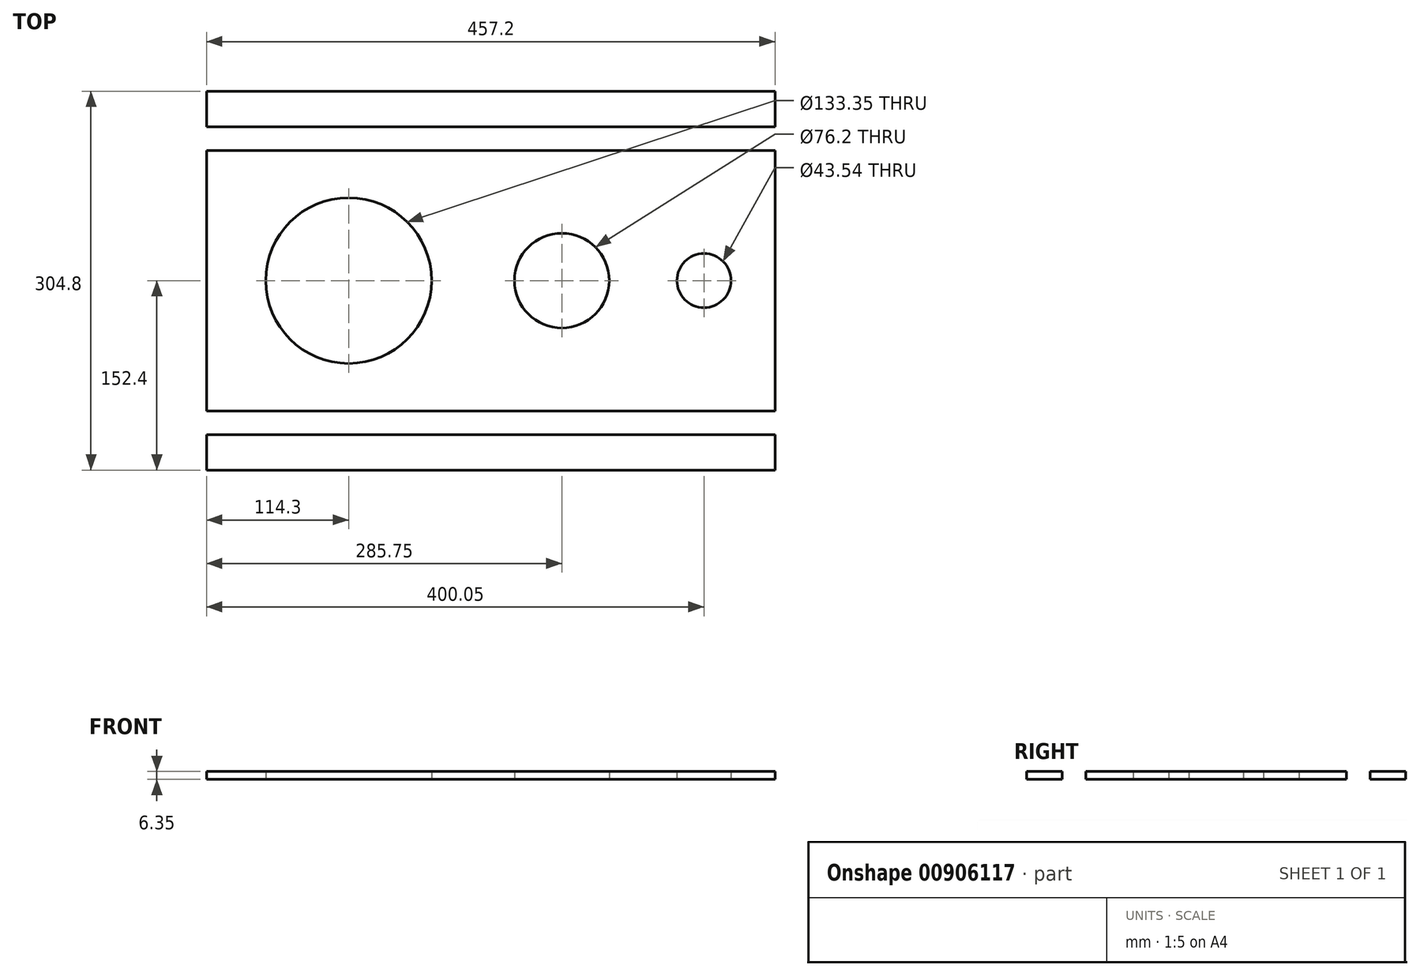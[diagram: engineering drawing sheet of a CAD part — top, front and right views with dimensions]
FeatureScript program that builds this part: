
annotation { "Feature Type Name" : "Feature", "Feature Type Description" : "" }
export const myFeature = defineFeature(function(context is Context, id is Id, definition is map)
    precondition{}
    {
        {
            var Q0;
            Q0=qCreatedBy(makeId("Top.planeOp"),FACE);
            var sketch = newSketch(context, id + "F0", { "sketchPlane" : qUnion([Q0])});
            skCircle(sketch, "E0", {"center": v(0, 0) * mm, "radius": 25.4 * mm, "construction": true});
            skCircle(sketch, "E1.cCircle", {"center": v(0, 0) * mm, "radius": 42.94 * mm, "construction": true});
            skLineSegment(sketch, "E1.0", {"start": v(0, 44.45) * mm, "end": v(22.22, 38.5) * mm, "construction": true});
            skLineSegment(sketch, "E1.1", {"start": v(22.22, 38.5) * mm, "end": v(38.5, 22.23) * mm, "construction": true});
            skLineSegment(sketch, "E1.2", {"start": v(38.5, 22.22) * mm, "end": v(44.45, 0) * mm, "construction": true});
            skLineSegment(sketch, "E1.3", {"start": v(44.45, 0) * mm, "end": v(38.5, -22.22) * mm, "construction": true});
            skLineSegment(sketch, "E1.4", {"start": v(38.5, -22.22) * mm, "end": v(22.23, -38.5) * mm, "construction": true});
            skLineSegment(sketch, "E1.5", {"start": v(22.23, -38.5) * mm, "end": v(0, -44.45) * mm, "construction": true});
            skLineSegment(sketch, "E1.6", {"start": v(0, -44.45) * mm, "end": v(-22.22, -38.5) * mm, "construction": true});
            skLineSegment(sketch, "E1.7", {"start": v(-22.22, -38.5) * mm, "end": v(-38.5, -22.23) * mm, "construction": true});
            skLineSegment(sketch, "E1.8", {"start": v(-38.5, -22.23) * mm, "end": v(-44.45, 0) * mm, "construction": true});
            skLineSegment(sketch, "E1.9", {"start": v(-44.45, 0) * mm, "end": v(-38.5, 22.22) * mm, "construction": true});
            skLineSegment(sketch, "E1.10", {"start": v(-38.5, 22.22) * mm, "end": v(-22.22, 38.5) * mm, "construction": true});
            skLineSegment(sketch, "E1.11", {"start": v(-22.22, 38.5) * mm, "end": v(0, 44.45) * mm, "construction": true});
            skPoint(sketch, "E1.0.midPoint", {"position": v(11.11, 41.47) * mm});
            skCircle(sketch, "E2", {"center": v(22.22, 38.5) * mm, "radius": 9.53 * mm, "construction": true});
            skCircle(sketch, "E3", {"center": v(38.5, 22.23) * mm, "radius": 9.53 * mm, "construction": true});
            skCircle(sketch, "E4", {"center": v(44.45, 0) * mm, "radius": 9.53 * mm, "construction": true});
            skCircle(sketch, "E5", {"center": v(38.5, -22.22) * mm, "radius": 9.53 * mm, "construction": true});
            skCircle(sketch, "E6", {"center": v(22.23, -38.5) * mm, "radius": 9.53 * mm, "construction": true});
            skPoint(sketch, "E7.startSnap0", {"position": v(-41.47, 11.11) * mm});
            skArc(sketch, "E8", {"start": v(0, 45.72) * mm, "mid": v(-45.72, 0) * mm, "end": v(0, -45.72) * mm, "construction": true});
            skArc(sketch, "E9.0.startCap", {"start": v(0, 55.25) * mm, "mid": v(9.53, 45.72) * mm, "end": v(0, 36.2) * mm, "construction": true});
            skArc(sketch, "E9.0.endCap", {"start": v(0, -36.2) * mm, "mid": v(9.53, -45.72) * mm, "end": v(0, -55.25) * mm, "construction": true});
            skArc(sketch, "E9.0.left", {"start": v(0, 36.2) * mm, "mid": v(-36.2, 0) * mm, "end": v(0, -36.2) * mm, "construction": true});
            skArc(sketch, "E9.0.right", {"start": v(0, 55.25) * mm, "mid": v(-55.25, 0) * mm, "end": v(0, -55.25) * mm, "construction": true});
            skCircle(sketch, "E10", {"center": v(0, 0) * mm, "radius": 66.68 * mm});
            skCircle(sketch, "E11.0", {"center": v(0, 0) * mm, "radius": 73.03 * mm});
            skLineSegment(sketch, "E12.bottom", {"start": v(-114.3, 152.4) * mm, "end": v(107.95, 152.4) * mm});
            skLineSegment(sketch, "E12.top", {"start": v(-114.3, -152.4) * mm, "end": v(104.92, -152.4) * mm});
            skLineSegment(sketch, "E12.left", {"start": v(-114.3, 152.4) * mm, "end": v(-114.3, -152.4) * mm});
            skLineSegment(sketch, "E13", {"start": v(-114.3, 0) * mm, "end": v(114.3, 0) * mm, "construction": true});
            skLineSegment(sketch, "E14.bottom", {"start": v(107.95, 152.4) * mm, "end": v(342.9, 152.4) * mm});
            skLineSegment(sketch, "E14.top", {"start": v(104.92, -152.4) * mm, "end": v(342.9, -152.4) * mm});
            skLineSegment(sketch, "E14.right", {"start": v(342.9, 152.4) * mm, "end": v(342.9, -152.4) * mm});
            skLineSegment(sketch, "E15", {"start": v(342.9, 152.4) * mm, "end": v(495.3, 0) * mm});
            skLineSegment(sketch, "E16", {"start": v(495.3, 0) * mm, "end": v(342.9, -152.4) * mm});
            skLineSegment(sketch, "E17", {"start": v(-114.3, 123.83) * mm, "end": v(371.48, 123.83) * mm});
            skLineSegment(sketch, "E18", {"start": v(390.53, 104.78) * mm, "end": v(-114.3, 104.78) * mm});
            skLineSegment(sketch, "E19", {"start": v(-114.3, -104.77) * mm, "end": v(390.53, -104.77) * mm});
            skLineSegment(sketch, "E20", {"start": v(-114.3, -123.82) * mm, "end": v(371.48, -123.82) * mm});
            skLineSegment(sketch, "E21", {"start": v(114.3, 0) * mm, "end": v(495.3, 0) * mm, "construction": true});
            skCircle(sketch, "E22", {"center": v(171.45, 0) * mm, "radius": 38.1 * mm});
            skCircle(sketch, "E23", {"center": v(285.75, 0) * mm, "radius": 21.77 * mm});
            skCircle(sketch, "E24", {"center": v(387.35, 0) * mm, "radius": 12.7 * mm, "construction": true});
            skPoint(sketch, "E25", {"position": v(25.4, 0) * mm});
            skPoint(sketch, "E26", {"position": v(-25.4, 0) * mm});
            skLineSegment(sketch, "E27", {"start": v(-114.3, 152.4) * mm, "end": v(495.3, 0) * mm, "construction": true});
            skLineSegment(sketch, "E28", {"start": v(495.3, 0) * mm, "end": v(-114.3, -152.4) * mm, "construction": true});
            skSolve(sketch);
        }
        {
            var Q0;
            Q0=makeQuery(id+"F0.imprint","IMPRINT",FACE,{"disambiguationData":[TD([[makeQuery(id+"F0.imprint","IMPRINT",EDGE,{"derivedFrom":sQuery(id+"F0.wireOp",EDGE,"E9.0.startCap")}),-1.0]])]});
            var Q1;
            Q1=makeQuery(id+"F0.imprint","IMPRINT",FACE,{"disambiguationData":[TD([[makeQuery(id+"F0.imprint","IMPRINT",EDGE,{"derivedFrom":sQuery(id+"F0.wireOp",EDGE,"E0")}),1.0]])]});
            var Q2;
            Q2=makeQuery(id+"F0.imprint","IMPRINT",FACE,{"disambiguationData":[TD([[makeQuery(id+"F0.imprint","IMPRINT",EDGE,{"derivedFrom":sQuery(id+"F0.wireOp",EDGE,"E2")}),1.0]])]});
            var Q3;
            Q3=makeQuery(id+"F0.imprint","IMPRINT",FACE,{"disambiguationData":[TD([[makeQuery(id+"F0.imprint","IMPRINT",EDGE,{"derivedFrom":sQuery(id+"F0.wireOp",EDGE,"E3")}),1.0]])]});
            var Q4;
            Q4=makeQuery(id+"F0.imprint","IMPRINT",FACE,{"disambiguationData":[TD([[makeQuery(id+"F0.imprint","IMPRINT",EDGE,{"derivedFrom":sQuery(id+"F0.wireOp",EDGE,"E4")}),1.0]])]});
            var Q5;
            Q5=makeQuery(id+"F0.imprint","IMPRINT",FACE,{"disambiguationData":[TD([[makeQuery(id+"F0.imprint","IMPRINT",EDGE,{"derivedFrom":sQuery(id+"F0.wireOp",EDGE,"E5")}),1.0]])]});
            var Q6;
            Q6=makeQuery(id+"F0.imprint","IMPRINT",FACE,{"disambiguationData":[TD([[makeQuery(id+"F0.imprint","IMPRINT",EDGE,{"derivedFrom":sQuery(id+"F0.wireOp",EDGE,"E6")}),1.0]])]});
            var Q7;
            Q7=makeQuery(id+"F0.imprint","IMPRINT",FACE,{"disambiguationData":[TD([[makeQuery(id+"F0.imprint","IMPRINT",EDGE,{"derivedFrom":sQuery(id+"F0.wireOp",EDGE,"E10")}),-1.0]])]});
            extrude(context, id + "F1", {"entities" : qUnion([Q0, Q1, Q2, Q3, Q4, Q5, Q6, Q7]), "oppositeDirection" : true, "depth" : -6.35 * mm, "offsetDistance" : 25.4 * mm});
        }
        {
            var Q0;
            Q0=makeQuery(id+"F0.imprint","IMPRINT",FACE,{"disambiguationData":[TD([[makeQuery(id+"F0.imprint","IMPRINT",EDGE,{"derivedFrom":sQuery(id+"F0.wireOp",EDGE,"E11.0")}),-1.0]])]});
            var Q1;
            {var subQ1=sQuery(id+"F0.wireOp",EDGE,"E12.left");var subQ3=sQuery(id+"F0.wireOp",EDGE,"E20");var subQ4=makeQuery(id+"F0.imprint","INTERSECT",VERTEX,{"derivedFrom":[subQ1,subQ3]});Q1=makeQuery(id+"F0.imprint","IMPRINT",FACE,{"disambiguationData":[TD([[makeQuery(id+"F0.imprint","IMPRINT",EDGE,{"disambiguationData":[TD([[subQ4,-1.0]])],"derivedFrom":subQ3}),-1.0]])]});}
            var Q2;
            {var subQ1=sQuery(id+"F0.wireOp",EDGE,"E12.left");var subQ3=sQuery(id+"F0.wireOp",EDGE,"E17");var subQ4=makeQuery(id+"F0.imprint","INTERSECT",VERTEX,{"derivedFrom":[subQ1,subQ3]});Q2=makeQuery(id+"F0.imprint","IMPRINT",FACE,{"disambiguationData":[TD([[makeQuery(id+"F0.imprint","IMPRINT",EDGE,{"disambiguationData":[TD([[subQ4,-1.0]])],"derivedFrom":subQ3}),1.0]])]});}
            extrude(context, id + "F2", {"entities" : qUnion([Q0, Q1, Q2]), "operationType" : NewBodyOperationType.ADD, "depth" : 6.35 * mm, "offsetDistance" : 25.4 * mm});
        }
    });
